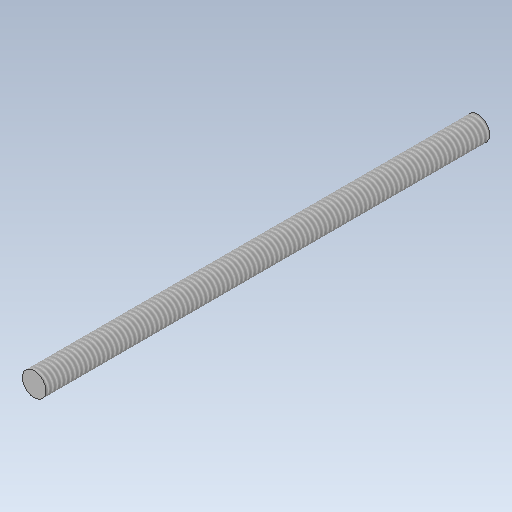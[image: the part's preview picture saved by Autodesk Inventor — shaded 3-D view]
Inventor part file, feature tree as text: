
AUTODESK INVENTOR PART (.ipt)
format: ipt  version: 2020 (Build 240168000, 168)  size: 106,496 bytes
history: native  units: mm
features: extrude x1, thread x1, sketch x1
ambient origin geometry x8: Origin, YZ Plane, XZ Plane, XY Plane, X Axis, Y Axis, Z Axis, Center Point
bodies: Solid1 (feature_tree)
feature tree (3):
  extrude  "Extrusion1"  Depth=150.0mm TaperAngle=0.0deg
  thread  "Thread1"  [1 undecoded]
  sketch  "Sketch1"  dims[d0=8.0mm d1=150.0mm d2=0.0mm d3=550.0mm d4=0.0mm]
note: 1 required parameter value undecoded (feature->parameter linkage not recoverable at this tier; creation-order binding heuristic only, values carry confidence <= 0.55)
